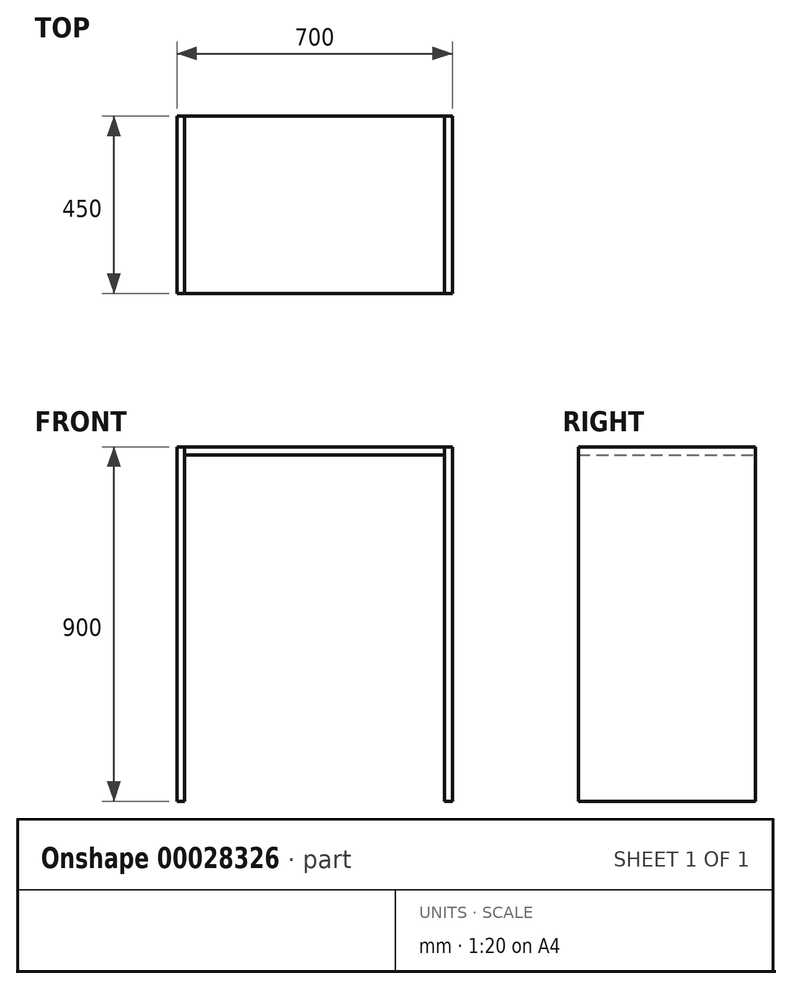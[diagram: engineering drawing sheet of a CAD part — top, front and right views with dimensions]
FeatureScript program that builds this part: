
annotation { "Feature Type Name" : "Feature", "Feature Type Description" : "" }
export const myFeature = defineFeature(function(context is Context, id is Id, definition is map)
    precondition{}
    {
        {
            var Q0;
            Q0=qCreatedBy(makeId("Top.planeOp"),FACE);
            var sketch = newSketch(context, id + "F0", { "sketchPlane" : qUnion([Q0])});
            skLineSegment(sketch, "E0.bottom", {"start": v(-294.4, 225.48) * mm, "end": v(-274.4, 225.48) * mm});
            skLineSegment(sketch, "E0.top", {"start": v(-294.4, -224.52) * mm, "end": v(-274.4, -224.52) * mm});
            skLineSegment(sketch, "E0.left", {"start": v(-294.4, 225.48) * mm, "end": v(-294.4, -224.52) * mm});
            skLineSegment(sketch, "E0.right", {"start": v(-274.4, 225.48) * mm, "end": v(-274.4, -224.52) * mm});
            skLineSegment(sketch, "E1.left", {"start": v(385.6, 225.48) * mm, "end": v(385.6, -224.52) * mm});
            skLineSegment(sketch, "E1.right", {"start": v(405.6, 225.48) * mm, "end": v(405.6, -224.52) * mm});
            skLineSegment(sketch, "E1.top", {"start": v(385.6, -224.52) * mm, "end": v(405.6, -224.52) * mm});
            skLineSegment(sketch, "E1.bottom", {"start": v(385.6, 225.48) * mm, "end": v(405.6, 225.48) * mm});
            skSolve(sketch);
        }
        {
            var Q0;
            Q0=qSketchRegion(id+"F0",true);
            extrude(context, id + "F1", {"entities" : qUnion([Q0]), "depth" : 900 * mm});
        }
        {
            var Q0;
            Q0=makeQuery(id+"F1.opExtrude","SWEPT_FACE",FACE,{"disambiguationData":[OSD([sQuery(id+"F0.wireOp",EDGE,"E0.right")])]});
            var sketch = newSketch(context, id + "F2", { "sketchPlane" : qUnion([Q0])});
            skLineSegment(sketch, "E2.bottom", {"start": v(-224.52, 900) * mm, "end": v(225.48, 900) * mm});
            skLineSegment(sketch, "E2.top", {"start": v(-224.52, 880) * mm, "end": v(225.48, 880) * mm});
            skLineSegment(sketch, "E2.left", {"start": v(-224.52, 900) * mm, "end": v(-224.52, 880) * mm});
            skLineSegment(sketch, "E2.right", {"start": v(225.48, 900) * mm, "end": v(225.48, 880) * mm});
            skSolve(sketch);
        }
        {
            var Q0;
            Q0=qSketchRegion(id+"F2",true);
            var Q1;
            Q1=makeQuery(id+"F1.opExtrude","SWEPT_FACE",FACE,{"disambiguationData":[OSD([sQuery(id+"F0.wireOp",EDGE,"E1.left")])]});
            extrude(context, id + "F3", {"entities" : qUnion([Q0]), "endBound" : BoundingType.UP_TO_SURFACE, "endBoundEntityFace" : qUnion([Q1]), "depth" : 25 * mm});
        }
    });
